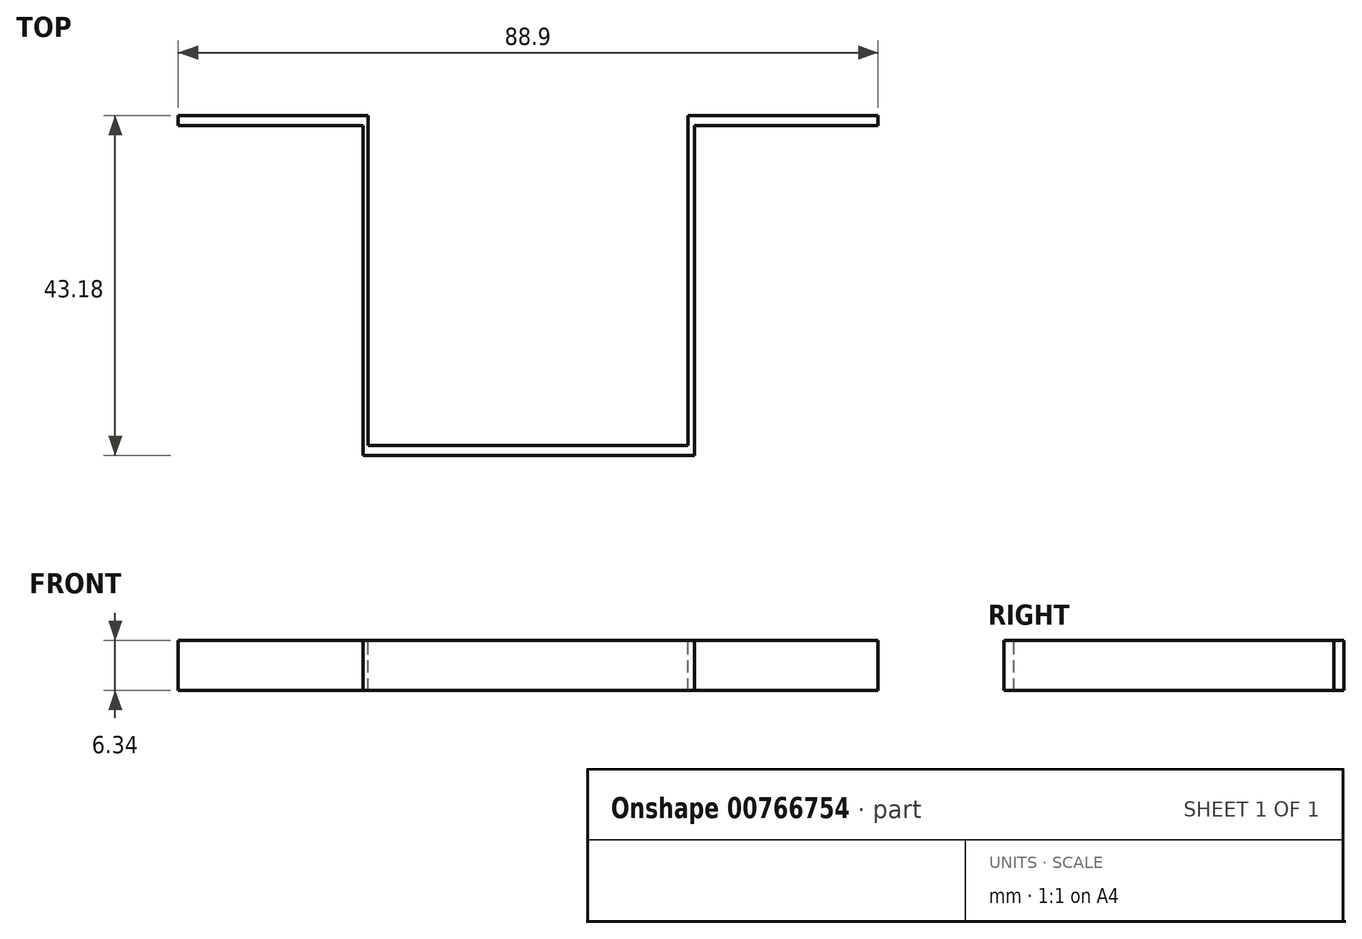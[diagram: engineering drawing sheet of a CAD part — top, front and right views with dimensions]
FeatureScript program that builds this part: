
annotation { "Feature Type Name" : "Feature", "Feature Type Description" : "" }
export const myFeature = defineFeature(function(context is Context, id is Id, definition is map)
    precondition{}
    {
        {
            var Q0;
            Q0=qCreatedBy(makeId("Front.planeOp"),FACE);
            var sketch = newSketch(context, id + "F0", { "sketchPlane" : qUnion([Q0])});
            skLineSegment(sketch, "E0.bottom", {"start": v(44.45, 3.18) * mm, "end": v(-44.45, 3.18) * mm});
            skLineSegment(sketch, "E0.top", {"start": v(44.45, -3.18) * mm, "end": v(-44.45, -3.18) * mm});
            skLineSegment(sketch, "E0.left", {"start": v(44.45, 3.18) * mm, "end": v(44.45, -3.18) * mm});
            skLineSegment(sketch, "E0.right", {"start": v(-44.45, 3.18) * mm, "end": v(-44.45, -3.18) * mm});
            skPoint(sketch, "E0.middle", {"position": v(0, 0) * mm});
            skSolve(sketch);
        }
        {
            var Q0;
            Q0=makeQuery(id+"F0.imprint","IMPRINT",FACE,{"disambiguationData":[TD([[makeQuery(id+"F0.imprint","IMPRINT",EDGE,{"derivedFrom":sQuery(id+"F0.wireOp",EDGE,"E0.bottom")}),1.0]])]});
            extrude(context, id + "F1", {"entities" : qUnion([Q0]), "depth" : 43.18 * mm, "offsetDistance" : 25.4 * mm});
        }
        {
            var Q0;
            Q0=makeQuery(id+"F1.opExtrude","CAP_FACE",FACE,{"disambiguationData":[OSD([sQuery(id+"F0.wireOp",EDGE,"E0.bottom"),sQuery(id+"F0.wireOp",EDGE,"E0.top"),sQuery(id+"F0.wireOp",EDGE,"E0.left"),sQuery(id+"F0.wireOp",EDGE,"E0.right")])],"isStart":true});
            var sketch = newSketch(context, id + "F2", { "sketchPlane" : qUnion([Q0])});
            skLineSegment(sketch, "E1.bottom", {"start": v(20.32, -3.18) * mm, "end": v(-20.32, -3.18) * mm});
            skLineSegment(sketch, "E1.top", {"start": v(20.32, 3.18) * mm, "end": v(-20.32, 3.18) * mm});
            skLineSegment(sketch, "E1.left", {"start": v(20.32, -3.18) * mm, "end": v(20.32, 3.18) * mm});
            skLineSegment(sketch, "E1.right", {"start": v(-20.32, -3.18) * mm, "end": v(-20.32, 3.18) * mm});
            skPoint(sketch, "E1.middle", {"position": v(0, 0) * mm});
            skSolve(sketch);
        }
        {
            var Q0;
            Q0=makeQuery(id+"F2.imprint","IMPRINT",FACE,{"disambiguationData":[TD([[makeQuery(id+"F2.imprint","IMPRINT",EDGE,{"derivedFrom":sQuery(id+"F2.wireOp",EDGE,"E1.bottom")}),1.0]])]});
            extrude(context, id + "F3", {"entities" : qUnion([Q0]), "operationType" : NewBodyOperationType.REMOVE, "oppositeDirection" : true, "depth" : 41.9 * mm, "offsetDistance" : 25.4 * mm});
        }
        {
            var Q0;
            Q0=makeQuery(id+"F1.opExtrude","CAP_FACE",FACE,{"disambiguationData":[OSD([sQuery(id+"F0.wireOp",EDGE,"E0.bottom"),sQuery(id+"F0.wireOp",EDGE,"E0.top"),sQuery(id+"F0.wireOp",EDGE,"E0.left"),sQuery(id+"F0.wireOp",EDGE,"E0.right")])],"isStart":false});
            var sketch = newSketch(context, id + "F4", { "sketchPlane" : qUnion([Q0])});
            skLineSegment(sketch, "E2.bottom", {"start": v(-20.95, 3.18) * mm, "end": v(-44.5, 3.18) * mm});
            skLineSegment(sketch, "E2.top", {"start": v(-20.95, -3.18) * mm, "end": v(-44.5, -3.18) * mm});
            skLineSegment(sketch, "E2.left", {"start": v(-20.95, 3.18) * mm, "end": v(-20.95, -3.18) * mm});
            skLineSegment(sketch, "E2.right", {"start": v(-44.5, 3.18) * mm, "end": v(-44.5, -3.18) * mm});
            skSolve(sketch);
        }
        {
            var Q0;
            Q0=makeQuery(id+"F4.imprint","IMPRINT",FACE,{"disambiguationData":[TD([[makeQuery(id+"F4.imprint","IMPRINT",EDGE,{"derivedFrom":sQuery(id+"F4.wireOp",EDGE,"E2.bottom")}),1.0]])]});
            extrude(context, id + "F5", {"entities" : qUnion([Q0]), "operationType" : NewBodyOperationType.REMOVE, "oppositeDirection" : true, "depth" : 41.9 * mm, "offsetDistance" : 25.4 * mm});
        }
        {
            var Q0;
            Q0=makeQuery(id+"F1.opExtrude","CAP_FACE",FACE,{"disambiguationData":[OSD([sQuery(id+"F0.wireOp",EDGE,"E0.bottom"),sQuery(id+"F0.wireOp",EDGE,"E0.top"),sQuery(id+"F0.wireOp",EDGE,"E0.left"),sQuery(id+"F0.wireOp",EDGE,"E0.right")])],"isStart":false});
            var sketch = newSketch(context, id + "F6", { "sketchPlane" : qUnion([Q0])});
            skLineSegment(sketch, "E3.bottom", {"start": v(44.45, -3.18) * mm, "end": v(21.13, -3.18) * mm});
            skLineSegment(sketch, "E3.top", {"start": v(44.45, 3.18) * mm, "end": v(21.13, 3.18) * mm});
            skLineSegment(sketch, "E3.left", {"start": v(44.45, -3.18) * mm, "end": v(44.45, 3.18) * mm});
            skLineSegment(sketch, "E3.right", {"start": v(21.13, -3.18) * mm, "end": v(21.13, 3.18) * mm});
            skSolve(sketch);
        }
        {
            var Q0;
            Q0=makeQuery(id+"F6.imprint","IMPRINT",FACE,{"disambiguationData":[TD([[makeQuery(id+"F6.imprint","IMPRINT",EDGE,{"derivedFrom":sQuery(id+"F6.wireOp",EDGE,"E3.bottom")}),-1.0]])]});
            extrude(context, id + "F7", {"entities" : qUnion([Q0]), "operationType" : NewBodyOperationType.REMOVE, "oppositeDirection" : true, "depth" : 41.9 * mm, "offsetDistance" : 25.4 * mm});
        }
    });
